# Revit family: IEK_Держатель для мачты опорный_40 мм_Для плоской кровли
name_source: partatom
category: Обобщенные модели
units: mm (PartAtom-declared; Revit-internal decimal feet)

## family parameters
Может служить основой для арматурных стержней = Нет
Общий = Да
Основа = Грань
При загрузке вырезать с полостями = Нет
Размер круглого соединителя = Использовать диаметр
Тип детали = Нормальный
Точка расчета площади = Нет

## types (1)
- 40 мм_450 мм
    ADSK_URL страницы изделия = https://www.iek.ru
    ADSK_Версия Revit = 2019
    ADSK_Версия семейства = 1.0
    ADSK_Группирование = VIII. ЭЛЕМЕНТЫ ВНЕШНЕЙ МОЛНИЕЗАЩИТЫ
    ADSK_Единица измерения = шт
    ADSK_Завод-изготовитель = IEK
    ADSK_Код изделия = ZML10D-MH-04-040
    ADSK_Масса = 1.8
    ADSK_Материал = Окраска - RAL 7035, светло-серый
    ADSK_Материал наименование = Сталь оцинкованная
    ADSK_Наименование = Держатель мачты 40мм опорный для плоской кровли IEK
    IEK_URL = https://www.iek.ru
    IEK_Описание = Держатель мачты 40 мм опорный для плоской кровли товарного знака IEK используется надежной установки молниеприемных мачт на плоскую кровлю зданий и сооружений.
    IEK_Цена за единицу = 2678
    KSI_CMa_Строительные материалы = 24.10.35.000.08.3.05.06-0001
    Отметка по умолчанию = 0 мм

## geometry (parser evidence)
native form markers: Blend x1
no freeform markers — native parametric forms only
